# Revit family: HTT31
name_source: partatom
category: Detail Items
revit_build: Autodesk Revit 2014 (Build: 20130308_1515(x64)
units: mm (PartAtom-declared; Revit-internal decimal feet)

## types (4) — shared parameters
A = 793 mm
B = 57 mm
C = 54 mm
D = 12 mm  [stored 0.0393701 ft]
Description = ***
E = 33 mm
F = 80 mm
Manufacturer = Simpson Strong-Tie Company Inc.
Model = HTT31
Model Disclaimer = Contact Simpson Strong-Tie Company Inc. for more information
Product Type = Holdown
Provide Feedback = http://www.strongtie.com
URL = https://www.strongtie.eu
t = 3 mm  [stored 0.00984252 ft]

## per-type parameters (varying)
| type | _visiblefront | _visibleleft | _visibleright | _visibletop |
| SST_HTT31_Front View | Yes | No | No | No |
| SST_HTT31_Top View | No | No | No | Yes |
| SST_HTT31_Left View | No | Yes | No | No |
| SST_HTT31_Right View | No | No | Yes | No |

note: [stored X ft] marks values corroborated as IEEE doubles in the binary element streams (Revit-internal decimal feet)
